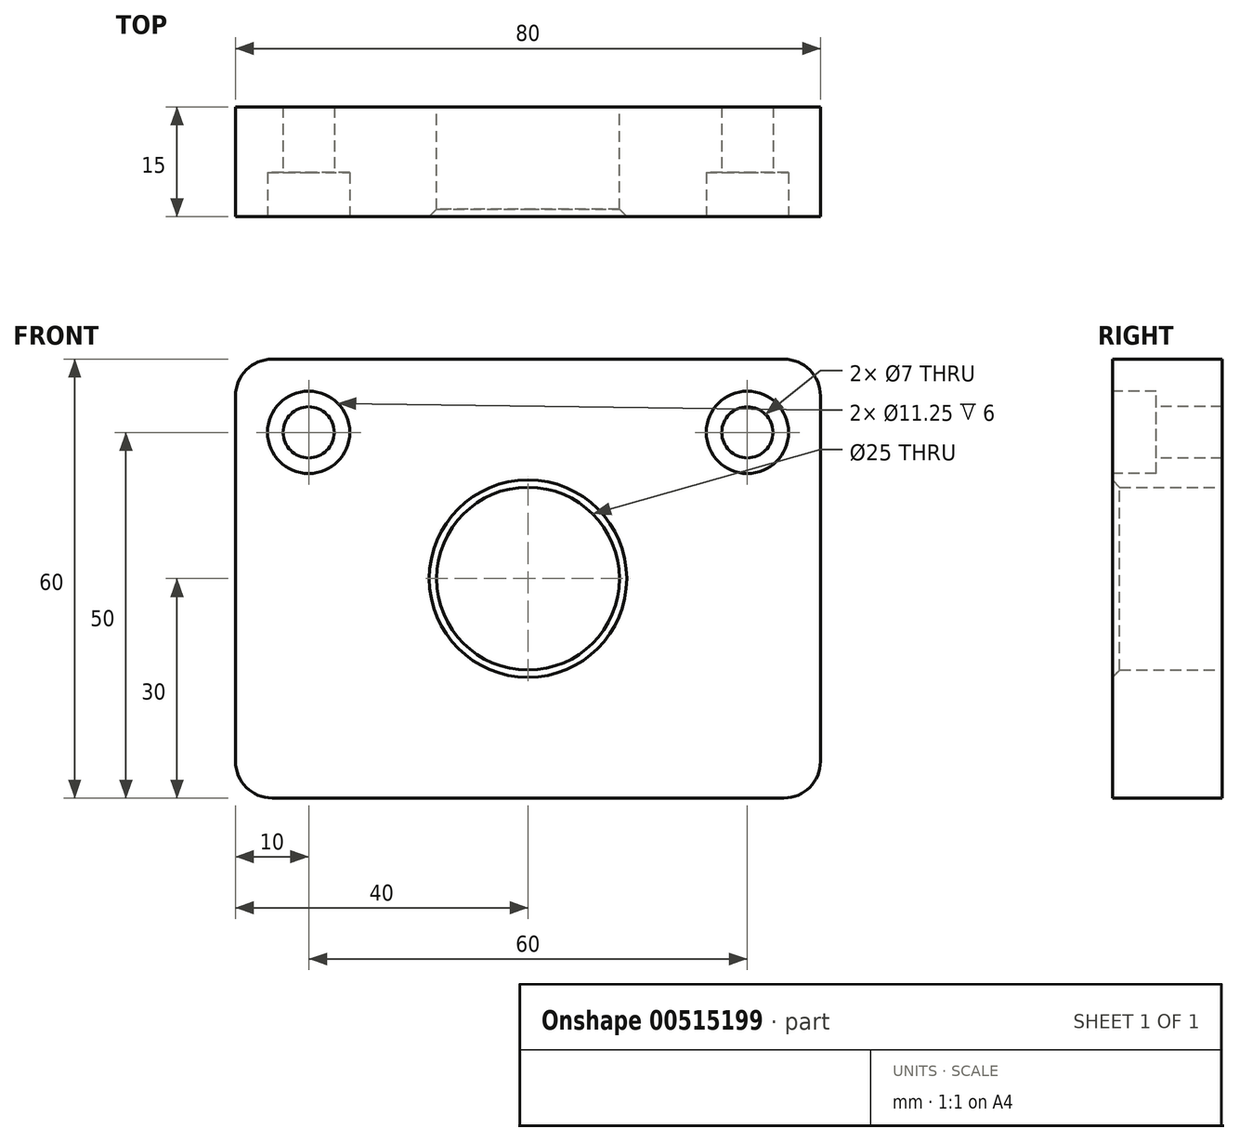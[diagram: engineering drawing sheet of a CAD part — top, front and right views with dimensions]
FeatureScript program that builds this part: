
annotation { "Feature Type Name" : "Feature", "Feature Type Description" : "" }
export const myFeature = defineFeature(function(context is Context, id is Id, definition is map)
    precondition{}
    {
        {
            var Q0;
            Q0=qCreatedBy(makeId("Front.planeOp"),FACE);
            var sketch = newSketch(context, id + "F0", { "sketchPlane" : qUnion([Q0])});
            skLineSegment(sketch, "E0.bottom", {"start": v(40, 30) * mm, "end": v(-40, 30) * mm});
            skLineSegment(sketch, "E0.top", {"start": v(40, -30) * mm, "end": v(-40, -30) * mm});
            skLineSegment(sketch, "E0.left", {"start": v(40, 30) * mm, "end": v(40, -30) * mm});
            skLineSegment(sketch, "E0.right", {"start": v(-40, 30) * mm, "end": v(-40, -30) * mm});
            skPoint(sketch, "E0.middle", {"position": v(0, 0) * mm});
            skCircle(sketch, "E1", {"center": v(0, 0) * mm, "radius": 12.5 * mm});
            skSolve(sketch);
        }
        {
            var Q0;
            Q0=makeQuery(id+"F0.imprint","IMPRINT",FACE,{"disambiguationData":[TD([[makeQuery(id+"F0.imprint","IMPRINT",EDGE,{"derivedFrom":sQuery(id+"F0.wireOp",EDGE,"E0.bottom")}),1.0]])]});
            extrude(context, id + "F1", {"entities" : qUnion([Q0]), "depth" : 15 * mm, "offsetDistance" : 25 * mm});
        }
        {
            var Q0;
            Q0=makeQuery(id+"F1.opExtrude","CAP_FACE",FACE,{"disambiguationData":[OSD([sQuery(id+"F0.wireOp",EDGE,"E0.bottom"),sQuery(id+"F0.wireOp",EDGE,"E0.top"),sQuery(id+"F0.wireOp",EDGE,"E0.left"),sQuery(id+"F0.wireOp",EDGE,"E0.right"),sQuery(id+"F0.wireOp",EDGE,"E1")])],"isStart":false});
            var sketch = newSketch(context, id + "F2", { "sketchPlane" : qUnion([Q0])});
            skLineSegment(sketch, "E2", {"start": v(0, 37.55) * mm, "end": v(0, -41.64) * mm, "construction": true});
            skPoint(sketch, "E2.endSnap0", {"position": v(0, 30) * mm});
            skPoint(sketch, "E3", {"position": v(-30, 20) * mm});
            skPoint(sketch, "E4.MirrorP", {"position": v(30, 20) * mm});
            skSolve(sketch);
        }
        {
            var Q0;
            Q0=sQuery(id+"F2.wireOp",VERTEX,"E3");
            var Q1;
            Q1=sQuery(id+"F2.wireOp",VERTEX,"E4.MirrorP");
            var Q2;
            Q2=makeQuery(id+"F1.opExtrude","SWEPT_BODY",BODY,{"disambiguationData":[OSD([sQuery(id+"F0.wireOp",EDGE,"E0.bottom"),sQuery(id+"F0.wireOp",EDGE,"E0.top"),sQuery(id+"F0.wireOp",EDGE,"E0.left"),sQuery(id+"F0.wireOp",EDGE,"E0.right"),sQuery(id+"F0.wireOp",EDGE,"E1")])]});
            hole(context, id + "F3", {"style" : HoleStyle.C_BORE, "endStyle" : HoleEndStyle.THROUGH, "standardTappedOrClearance" : lookupTablePath({ "standard" : "ISO", "size" : "7", "type" : "Drilled" }), "standardBlindInLast" : lookupTablePath({ "standard" : "ISO", "size" : "7", "type" : "Drilled" }), "holeDiameter" : 7 * mm, "cBoreDiameter" : 11.25 * mm, "cBoreDepth" : 6 * mm, "tappedDepth" : 12 * mm, "tapClearance" : 3, "startFromSketch" : true, "locations" : qUnion([Q0, Q1]), "scope" : qUnion([Q2])});
        }
        {
            var Q0;
            Q0=makeQuery(id+"F1.opExtrude","SWEPT_EDGE",EDGE,{"disambiguationData":[OSD([sQuery(id+"F0.wireOp",EDGE,"E0.bottom"),sQuery(id+"F0.wireOp",EDGE,"E0.left")])]});
            var Q1;
            Q1=makeQuery(id+"F1.opExtrude","SWEPT_EDGE",EDGE,{"disambiguationData":[OSD([sQuery(id+"F0.wireOp",EDGE,"E0.top"),sQuery(id+"F0.wireOp",EDGE,"E0.left")])]});
            var Q2;
            Q2=makeQuery(id+"F1.opExtrude","SWEPT_EDGE",EDGE,{"disambiguationData":[OSD([sQuery(id+"F0.wireOp",EDGE,"E0.bottom"),sQuery(id+"F0.wireOp",EDGE,"E0.right")])]});
            var Q3;
            Q3=makeQuery(id+"F1.opExtrude","SWEPT_EDGE",EDGE,{"disambiguationData":[OSD([sQuery(id+"F0.wireOp",EDGE,"E0.top"),sQuery(id+"F0.wireOp",EDGE,"E0.right")])]});
            fillet(context, id + "F4", {"entities" : qUnion([Q0, Q1, Q2, Q3]), "radius" : 5 * mm, "tangentPropagation" : true, "allowEdgeOverflow" : false});
        }
        {
            var Q0;
            Q0=makeQuery(id+"F1.opExtrude","CAP_EDGE",EDGE,{"disambiguationData":[OSD([sQuery(id+"F0.wireOp",EDGE,"E1")])],"isStart":false});
            chamfer(context, id + "F5", {"entities" : qUnion([Q0]), "width" : 1 * mm, "tangentPropagation" : true});
        }
    });
